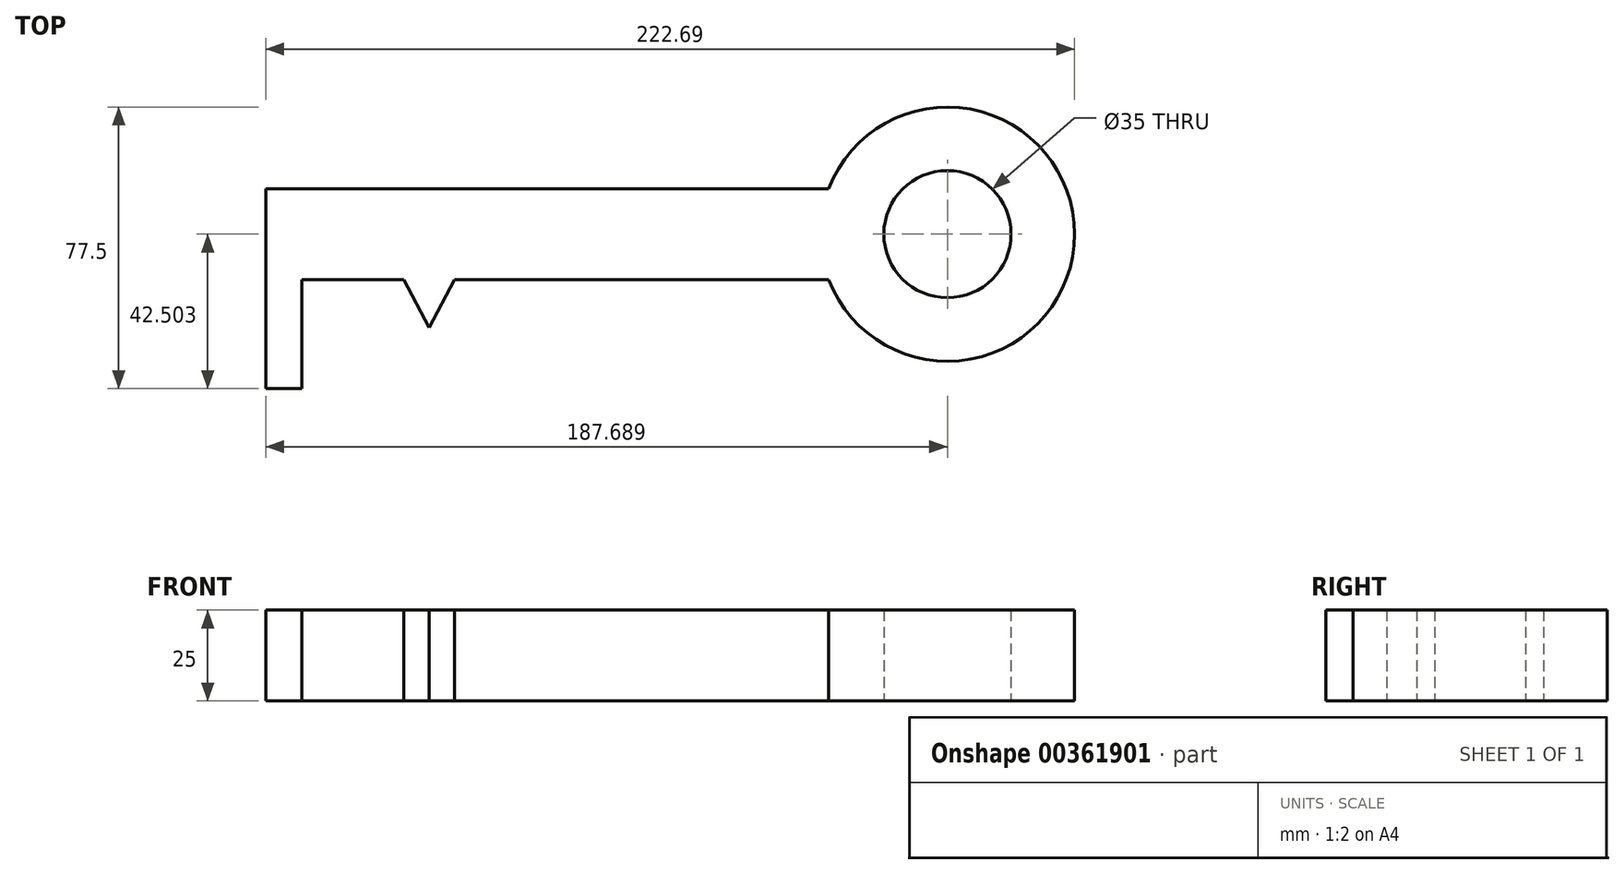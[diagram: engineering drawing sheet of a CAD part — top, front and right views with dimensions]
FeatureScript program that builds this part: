
annotation { "Feature Type Name" : "Feature", "Feature Type Description" : "" }
export const myFeature = defineFeature(function(context is Context, id is Id, definition is map)
    precondition{}
    {
        {
            var Q0;
            Q0=qCreatedBy(makeId("Top.planeOp"),FACE);
            var sketch = newSketch(context, id + "F0", { "sketchPlane" : qUnion([Q0])});
            skLineSegment(sketch, "E0.bottom", {"start": v(-63.72, 11.65) * mm, "end": v(91.28, 11.65) * mm});
            skLineSegment(sketch, "E0.top", {"start": v(-63.72, -13.35) * mm, "end": v(91.28, -13.35) * mm});
            skLineSegment(sketch, "E0.left", {"start": v(-63.72, 11.65) * mm, "end": v(-63.72, -13.35) * mm});
            skLineSegment(sketch, "E1.bottom", {"start": v(-63.72, -13.35) * mm, "end": v(-63.05, -13.35) * mm});
            skLineSegment(sketch, "E1.top", {"start": v(-63.72, -48.17) * mm, "end": v(-63.72, -48.17) * mm});
            skLineSegment(sketch, "E2.bottom", {"start": v(-63.72, -13.35) * mm, "end": v(-53.72, -13.35) * mm});
            skLineSegment(sketch, "E2.top", {"start": v(-63.72, -43.35) * mm, "end": v(-53.72, -43.35) * mm});
            skLineSegment(sketch, "E2.left", {"start": v(-63.72, -13.35) * mm, "end": v(-63.72, -43.35) * mm});
            skLineSegment(sketch, "E2.right", {"start": v(-53.72, -13.35) * mm, "end": v(-53.72, -43.35) * mm});
            skLineSegment(sketch, "E3.bottom", {"start": v(-43.72, -13.35) * mm, "end": v(-35.72, -13.35) * mm});
            skLineSegment(sketch, "E3.top", {"start": v(-43.72, -28.35) * mm, "end": v(-35.72, -28.35) * mm});
            skLineSegment(sketch, "E3.left", {"start": v(-43.72, -13.35) * mm, "end": v(-43.72, -28.35) * mm});
            skLineSegment(sketch, "E3.right", {"start": v(-35.72, -13.35) * mm, "end": v(-35.72, -28.35) * mm});
            skLineSegment(sketch, "E4", {"start": v(-25.72, -13.35) * mm, "end": v(-18.72, -26.61) * mm});
            skLineSegment(sketch, "E5", {"start": v(-18.72, -26.61) * mm, "end": v(-11.72, -13.35) * mm});
            skArc(sketch, "E6", {"start": v(91.28, -13.35) * mm, "mid": v(158.97, -0.85) * mm, "end": v(91.28, 11.65) * mm});
            skCircle(sketch, "E7", {"center": v(123.97, -0.85) * mm, "radius": 17.5 * mm});
            skLineSegment(sketch, "E8", {"start": v(-25.72, -13.35) * mm, "end": v(-11.72, -13.35) * mm});
            skSolve(sketch);
        }
        {
            var Q0;
            Q0=makeQuery(id+"F0.imprint","IMPRINT",FACE,{"disambiguationData":[TD([[makeQuery(id+"F0.imprint","IMPRINT",EDGE,{"derivedFrom":sQuery(id+"F0.wireOp",EDGE,"E2.top")}),1.0]])]});
            var Q1;
            Q1=makeQuery(id+"F0.imprint","IMPRINT",FACE,{"disambiguationData":[TD([[makeQuery(id+"F0.imprint","IMPRINT",EDGE,{"derivedFrom":sQuery(id+"F0.wireOp",EDGE,"E0.bottom")}),-1.0]])]});
            var Q2;
            Q2=makeQuery(id+"F0.imprint","IMPRINT",FACE,{"disambiguationData":[TD([[makeQuery(id+"F0.imprint","IMPRINT",EDGE,{"derivedFrom":sQuery(id+"F0.wireOp",EDGE,"E3.bottom")}),-1.0]])]});
            var Q3;
            Q3=makeQuery(id+"F0.imprint","IMPRINT",FACE,{"disambiguationData":[TD([[makeQuery(id+"F0.imprint","IMPRINT",EDGE,{"derivedFrom":sQuery(id+"F0.wireOp",EDGE,"E4")}),1.0]])]});
            extrude(context, id + "F1", {"entities" : qUnion([Q0, Q1, Q2, Q3]), "depth" : 25 * mm});
        }
    });
